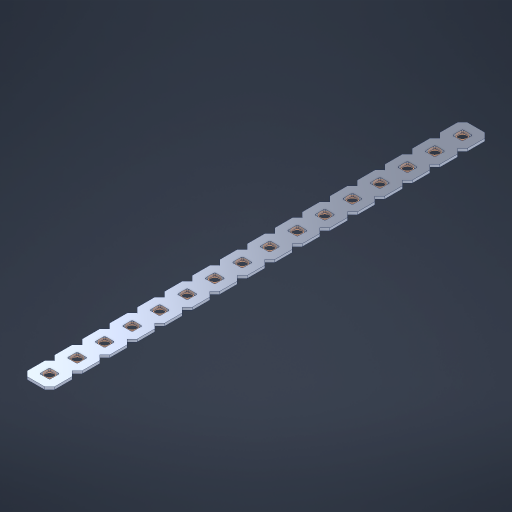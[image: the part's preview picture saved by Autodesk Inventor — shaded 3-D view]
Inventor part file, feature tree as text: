
AUTODESK INVENTOR PART (.ipt)
format: ipt  version: 2023 (Build 270158000, 158)  size: 465,920 bytes
history: native  units: in
note: dims shown in document units (in); Inventor stores cm internally (conversion verified against a paired STEP export)
features: other x17, extrude x15, sketch x2, pattern_linear x1
ambient origin geometry x8: Origin, YZ Plane, XZ Plane, XY Plane, X Axis, Y Axis, Z Axis, Center Point
bodies: Solid1 (feature_tree), Body (feature_tree)
feature tree (35):
  pattern_linear  "Rectangular Pattern1"  Spacing1=0.09in  [1 undecoded]
  sketch  "Sketch1"  dims[d1=0.5in]
  sketch  "Sketch2"  dims[d2=0.182in d3=0.09in d4=0.09in d5=0.09in d6=0.09in d7=0.09in d8=0.09in d9=0.09in d10=0.09in d11=0.02in d13=0.0in d14=0.172in d15=0.0625in d16=0.0in d19=0.5in d22=0.5in]
  other  "Srf1"
  other  "Srf126"
  other  "Srf127"
  other  "Srf128"
  other  "Srf129"
  other  "Srf130"
  other  "Srf131"
  other  "Srf250"
  other  "Srf251"
  other  "Srf252"
  other  "Srf253"
  other  "Srf254"
  other  "Srf255"
  other  "Srf256"
  other  "Srf257"
  other  "Srf258"
  other  "Circle"
  extrude  "ExtrusionSrf126"  Depth=0.09in
  extrude  "ExtrusionSrf127"  Depth=0.09in
  extrude  "ExtrusionSrf128"  Depth=0.09in
  extrude  "ExtrusionSrf129"  Depth=0.09in
  extrude  "ExtrusionSrf130"  Depth=0.09in
  extrude  "ExtrusionSrf131"  Depth=0.09in
  extrude  "ExtrusionSrf250"  Depth=0.09in
  extrude  "ExtrusionSrf251"  Depth=0.02in
  extrude  "ExtrusionSrf252"  TaperAngle=0.0deg  [1 undecoded]
  extrude  "ExtrusionSrf253"  Depth=0.5in
  extrude  "ExtrusionSrf254"  Depth=0.5in TaperAngle=0.0deg
  extrude  "ExtrusionSrf255"  Depth=0.5in
  extrude  "ExtrusionSrf256"  Depth=0.5in
  extrude  "ExtrusionSrf257"  [1 undecoded]
  extrude  "ExtrusionSrf258"  [1 undecoded]
note: 4 required parameter values undecoded (feature->parameter linkage not recoverable at this tier; creation-order binding heuristic only, values carry confidence <= 0.55)
